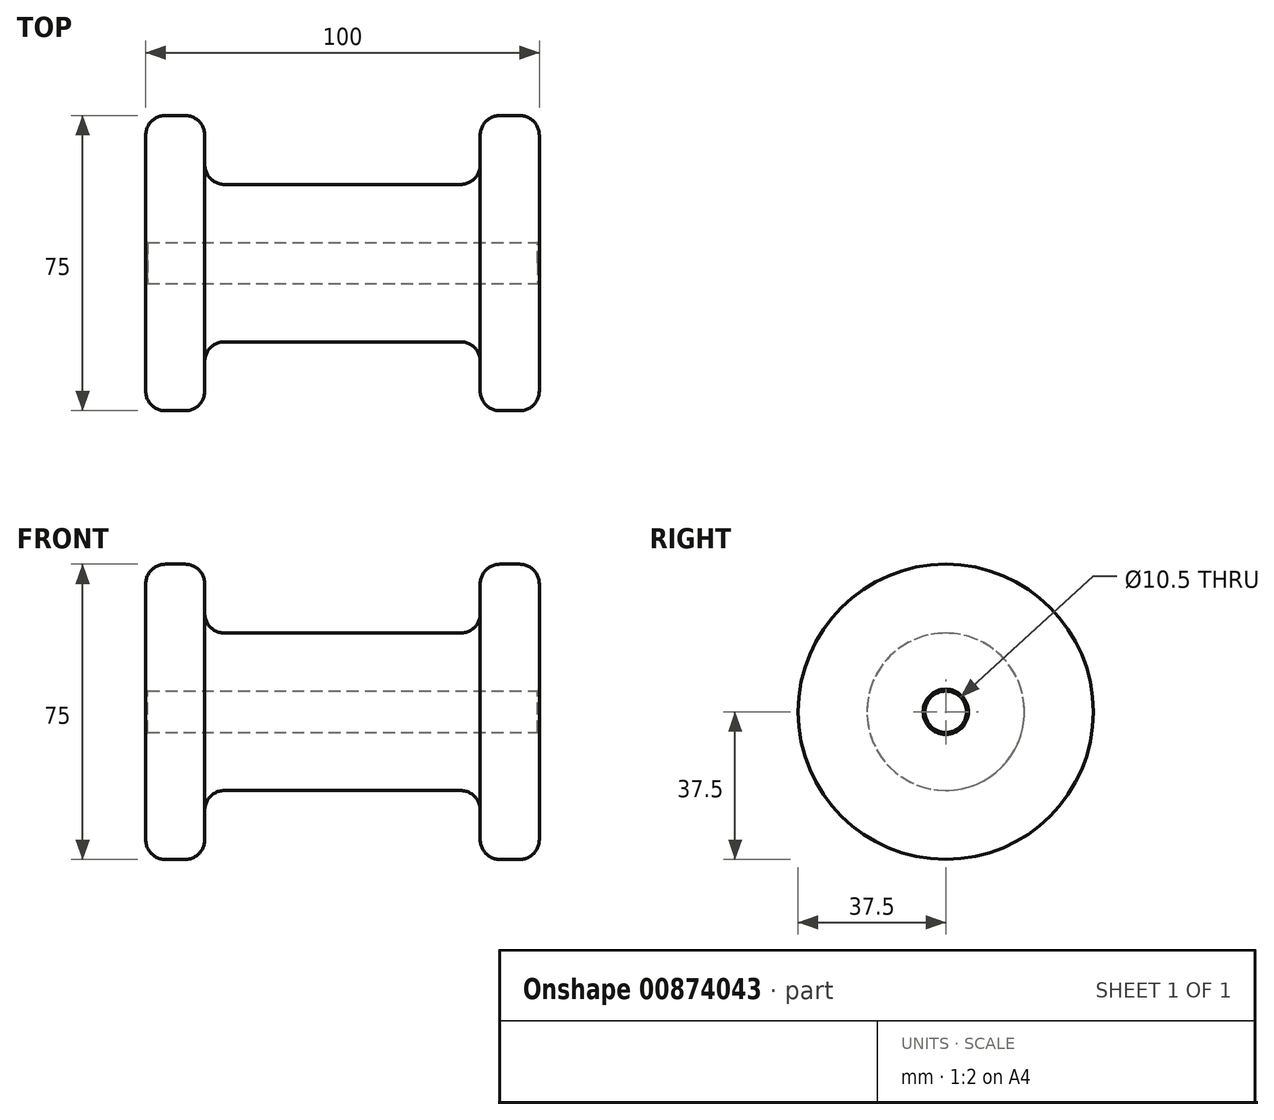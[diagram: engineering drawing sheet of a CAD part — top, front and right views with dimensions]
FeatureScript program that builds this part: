
annotation { "Feature Type Name" : "Feature", "Feature Type Description" : "" }
export const myFeature = defineFeature(function(context is Context, id is Id, definition is map)
    precondition{}
    {
        {
            var Q0;
            Q0=qCreatedBy(makeId("Top.planeOp"),FACE);
            var sketch = newSketch(context, id + "F0", { "sketchPlane" : qUnion([Q0])});
            skLineSegment(sketch, "E0", {"start": v(-26.08, 5.25) * mm, "end": v(-26.08, 37.5) * mm});
            skLineSegment(sketch, "E1", {"start": v(-26.08, 37.5) * mm, "end": v(-11.08, 37.5) * mm});
            skLineSegment(sketch, "E2", {"start": v(-11.08, 37.5) * mm, "end": v(-11.08, 20) * mm});
            skLineSegment(sketch, "E3", {"start": v(-11.08, 20) * mm, "end": v(58.92, 20) * mm});
            skLineSegment(sketch, "E4", {"start": v(58.92, 20) * mm, "end": v(58.92, 37.5) * mm});
            skLineSegment(sketch, "E5", {"start": v(58.92, 37.5) * mm, "end": v(73.92, 37.5) * mm});
            skLineSegment(sketch, "E6", {"start": v(73.92, 37.5) * mm, "end": v(73.92, 5.25) * mm});
            skLineSegment(sketch, "E7", {"start": v(-26.08, 5.25) * mm, "end": v(73.92, 5.25) * mm});
            skLineSegment(sketch, "E8", {"start": v(32.75, 0) * mm, "end": v(-39.25, 0) * mm});
            skPoint(sketch, "E9.orphan", {"position": v(-26.08, 0) * mm});
            skPoint(sketch, "E10.orphan", {"position": v(73.92, 0) * mm});
            skSolve(sketch);
        }
        {
            var Q0;
            Q0=makeQuery(id+"F0.imprint","IMPRINT",FACE,{"disambiguationData":[TD([[makeQuery(id+"F0.imprint","IMPRINT",EDGE,{"derivedFrom":sQuery(id+"F0.wireOp",EDGE,"E0")}),-1.0]])]});
            var Q1;
            Q1=sQuery(id+"F0.wireOp",EDGE,"E8");
            revolve(context, id + "F1", {"surfaceOperationType" : NewSurfaceOperationType.NEW, "entities" : qUnion([Q0]), "axis" : qUnion([Q1]), "revolveType" : RevolveType.FULL});
        }
        {
            var Q0;
            Q0=makeQuery(id+"F1.opRevolve","SWEPT_EDGE",EDGE,{"disambiguationData":[OSD([sQuery(id+"F0.wireOp",EDGE,"E0"),sQuery(id+"F0.wireOp",EDGE,"E1")])]});
            var Q1;
            Q1=makeQuery(id+"F1.opRevolve","SWEPT_EDGE",EDGE,{"disambiguationData":[OSD([sQuery(id+"F0.wireOp",EDGE,"E1"),sQuery(id+"F0.wireOp",EDGE,"E2")])]});
            var Q2;
            Q2=makeQuery(id+"F1.opRevolve","SWEPT_EDGE",EDGE,{"disambiguationData":[OSD([sQuery(id+"F0.wireOp",EDGE,"E4"),sQuery(id+"F0.wireOp",EDGE,"E5")])]});
            var Q3;
            Q3=makeQuery(id+"F1.opRevolve","SWEPT_EDGE",EDGE,{"disambiguationData":[OSD([sQuery(id+"F0.wireOp",EDGE,"E5"),sQuery(id+"F0.wireOp",EDGE,"E6")])]});
            var Q4;
            Q4=makeQuery(id+"F1.opRevolve","SWEPT_EDGE",EDGE,{"disambiguationData":[OSD([sQuery(id+"F0.wireOp",EDGE,"E3"),sQuery(id+"F0.wireOp",EDGE,"E4")])]});
            var Q5;
            Q5=makeQuery(id+"F1.opRevolve","SWEPT_FACE",FACE,{"disambiguationData":[OSD([sQuery(id+"F0.wireOp",EDGE,"E3")])]});
            fillet(context, id + "F2", {"entities" : qUnion([Q0, Q1, Q2, Q3, Q4, Q5]), "radius" : 5 * mm, "tangentPropagation" : true, "allowEdgeOverflow" : false});
        }
        {
            var Q0;
            Q0=makeQuery(id+"F1.opRevolve","SWEPT_EDGE",EDGE,{"disambiguationData":[OSD([sQuery(id+"F0.wireOp",EDGE,"E6"),sQuery(id+"F0.wireOp",EDGE,"E7")])]});
            var Q1;
            Q1=makeQuery(id+"F1.opRevolve","SWEPT_EDGE",EDGE,{"disambiguationData":[OSD([sQuery(id+"F0.wireOp",EDGE,"E0"),sQuery(id+"F0.wireOp",EDGE,"E7")])]});
            chamfer(context, id + "F3", {"entities" : qUnion([Q0, Q1]), "width" : 0.5 * mm, "tangentPropagation" : true});
        }
    });
